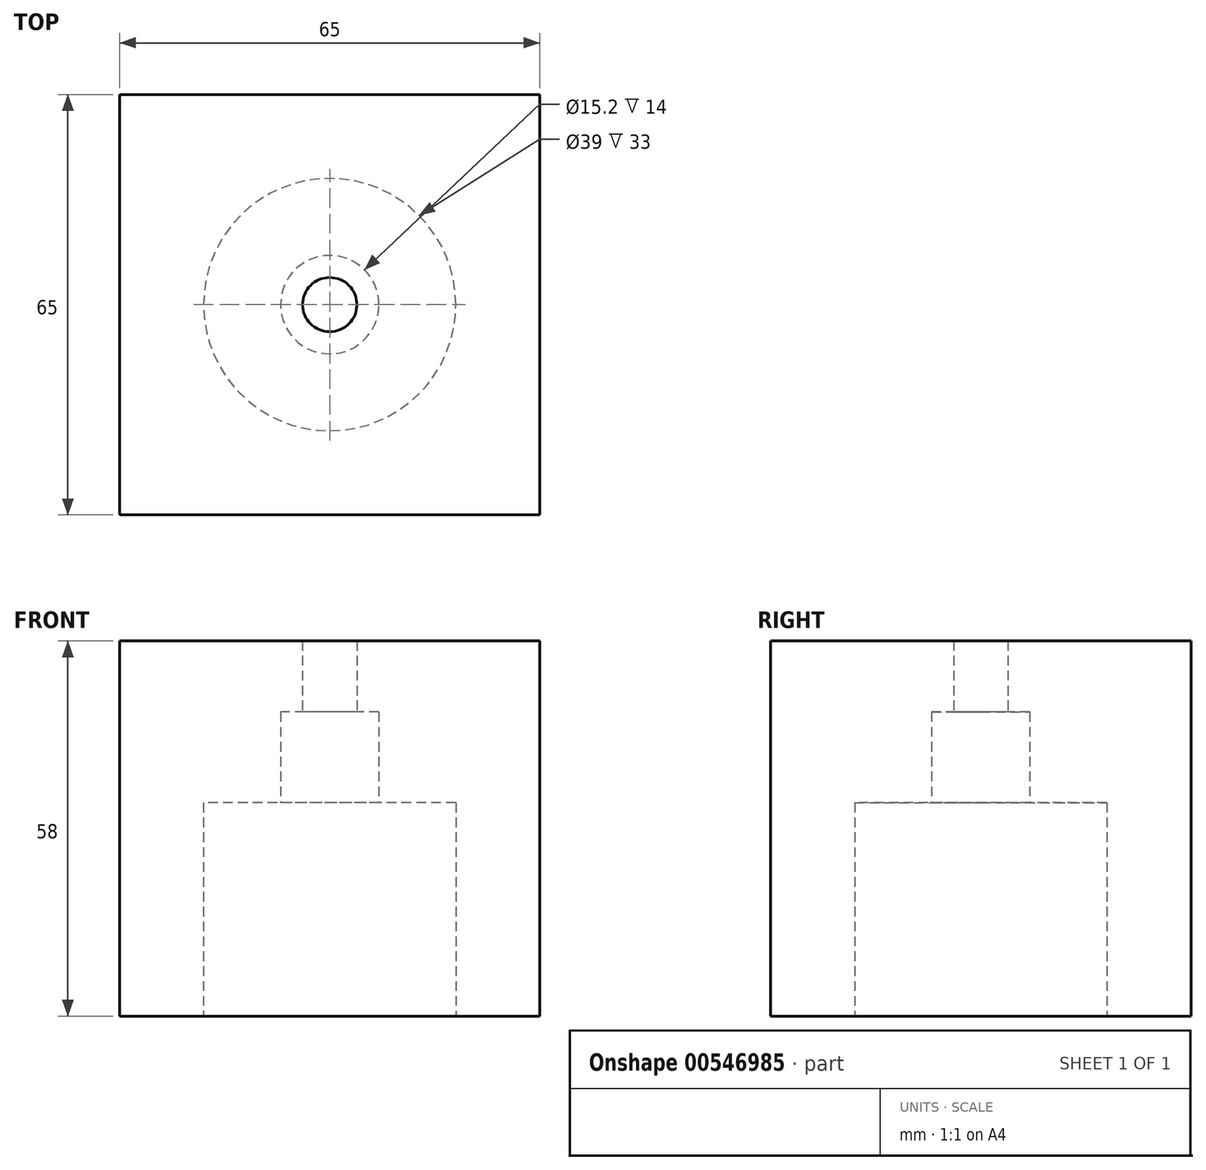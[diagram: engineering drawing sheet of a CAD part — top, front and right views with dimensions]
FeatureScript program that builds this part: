
annotation { "Feature Type Name" : "Feature", "Feature Type Description" : "" }
export const myFeature = defineFeature(function(context is Context, id is Id, definition is map)
    precondition{}
    {
        {
            var Q0;
            Q0=qCreatedBy(makeId("Top.planeOp"),FACE);
            var sketch = newSketch(context, id + "F0", { "sketchPlane" : qUnion([Q0])});
            skLineSegment(sketch, "E0.bottom", {"start": v(32.5, 32.5) * mm, "end": v(-32.5, 32.5) * mm});
            skLineSegment(sketch, "E0.top", {"start": v(32.5, -32.5) * mm, "end": v(-32.5, -32.5) * mm});
            skLineSegment(sketch, "E0.left", {"start": v(32.5, 32.5) * mm, "end": v(32.5, -32.5) * mm});
            skLineSegment(sketch, "E0.right", {"start": v(-32.5, 32.5) * mm, "end": v(-32.5, -32.5) * mm});
            skPoint(sketch, "E0.middle", {"position": v(0, 0) * mm});
            skSolve(sketch);
        }
        {
            var Q0;
            Q0=makeQuery(id+"F0.imprint","IMPRINT",FACE,{"disambiguationData":[TD([[makeQuery(id+"F0.imprint","IMPRINT",EDGE,{"derivedFrom":sQuery(id+"F0.wireOp",EDGE,"E0.bottom")}),1.0]])]});
            var sketch = newSketch(context, id + "F1", { "sketchPlane" : qUnion([Q0])});
            skCircle(sketch, "E1", {"center": v(0, 0) * mm, "radius": 25.5 * mm});
            skSolve(sketch);
        }
        {
            var Q0;
            Q0=qCreatedBy(makeId("Top.planeOp"),FACE);
            var sketch = newSketch(context, id + "F2", { "sketchPlane" : qUnion([Q0])});
            skCircle(sketch, "E2", {"center": v(0, 0) * mm, "radius": 19.5 * mm});
            skSolve(sketch);
        }
        {
            var Q0;
            Q0=qCreatedBy(makeId("Top.planeOp"),FACE);
            var sketch = newSketch(context, id + "F3", { "sketchPlane" : qUnion([Q0])});
            skCircle(sketch, "E3", {"center": v(0, 0) * mm, "radius": 4.2 * mm});
            skSolve(sketch);
        }
        {
            var Q0;
            Q0=qCreatedBy(makeId("Top.planeOp"),FACE);
            var sketch = newSketch(context, id + "F4", { "sketchPlane" : qUnion([Q0])});
            skCircle(sketch, "E4", {"center": v(0, 0) * mm, "radius": 7.6 * mm});
            skSolve(sketch);
        }
        {
            var Q0;
            Q0 = qSketchRegion(id + "F0", true);
            extrude(context, id + "F5", {"entities" : qUnion([Q0]), "depth" : 58 * mm, "offsetDistance" : 25 * mm});
        }
        {
            var Q0;
            Q0=makeQuery(id+"F1.imprint","IMPRINT",FACE,{"disambiguationData":[TD([[makeQuery(id+"F1.imprint","IMPRINT",EDGE,{"derivedFrom":sQuery(id+"F1.wireOp",EDGE,"E1")}),1.0]])]});
            extrude(context, id + "F6", {"entities" : qUnion([Q0]), "operationType" : NewBodyOperationType.ADD, "depth" : 25 * mm, "offsetDistance" : 25 * mm});
        }
        {
            var Q0;
            Q0=makeQuery(id+"F3.imprint","IMPRINT",FACE,{"disambiguationData":[TD([[makeQuery(id+"F3.imprint","IMPRINT",EDGE,{"derivedFrom":sQuery(id+"F3.wireOp",EDGE,"E3")}),1.0]])]});
            extrude(context, id + "F7", {"entities" : qUnion([Q0]), "operationType" : NewBodyOperationType.REMOVE, "depth" : 134 * mm, "offsetDistance" : 25 * mm});
        }
        {
            var Q0;
            Q0=makeQuery(id+"F4.imprint","IMPRINT",FACE,{"disambiguationData":[TD([[makeQuery(id+"F4.imprint","IMPRINT",EDGE,{"derivedFrom":sQuery(id+"F4.wireOp",EDGE,"E4")}),1.0]])]});
            extrude(context, id + "F8", {"entities" : qUnion([Q0]), "operationType" : NewBodyOperationType.REMOVE, "depth" : 47 * mm, "offsetDistance" : 25 * mm});
        }
        {
            var Q0;
            Q0 = qSketchRegion(id + "F2", true);
            extrude(context, id + "F9", {"entities" : qUnion([Q0]), "operationType" : NewBodyOperationType.REMOVE, "depth" : 33 * mm, "offsetDistance" : 25 * mm});
        }
    });
